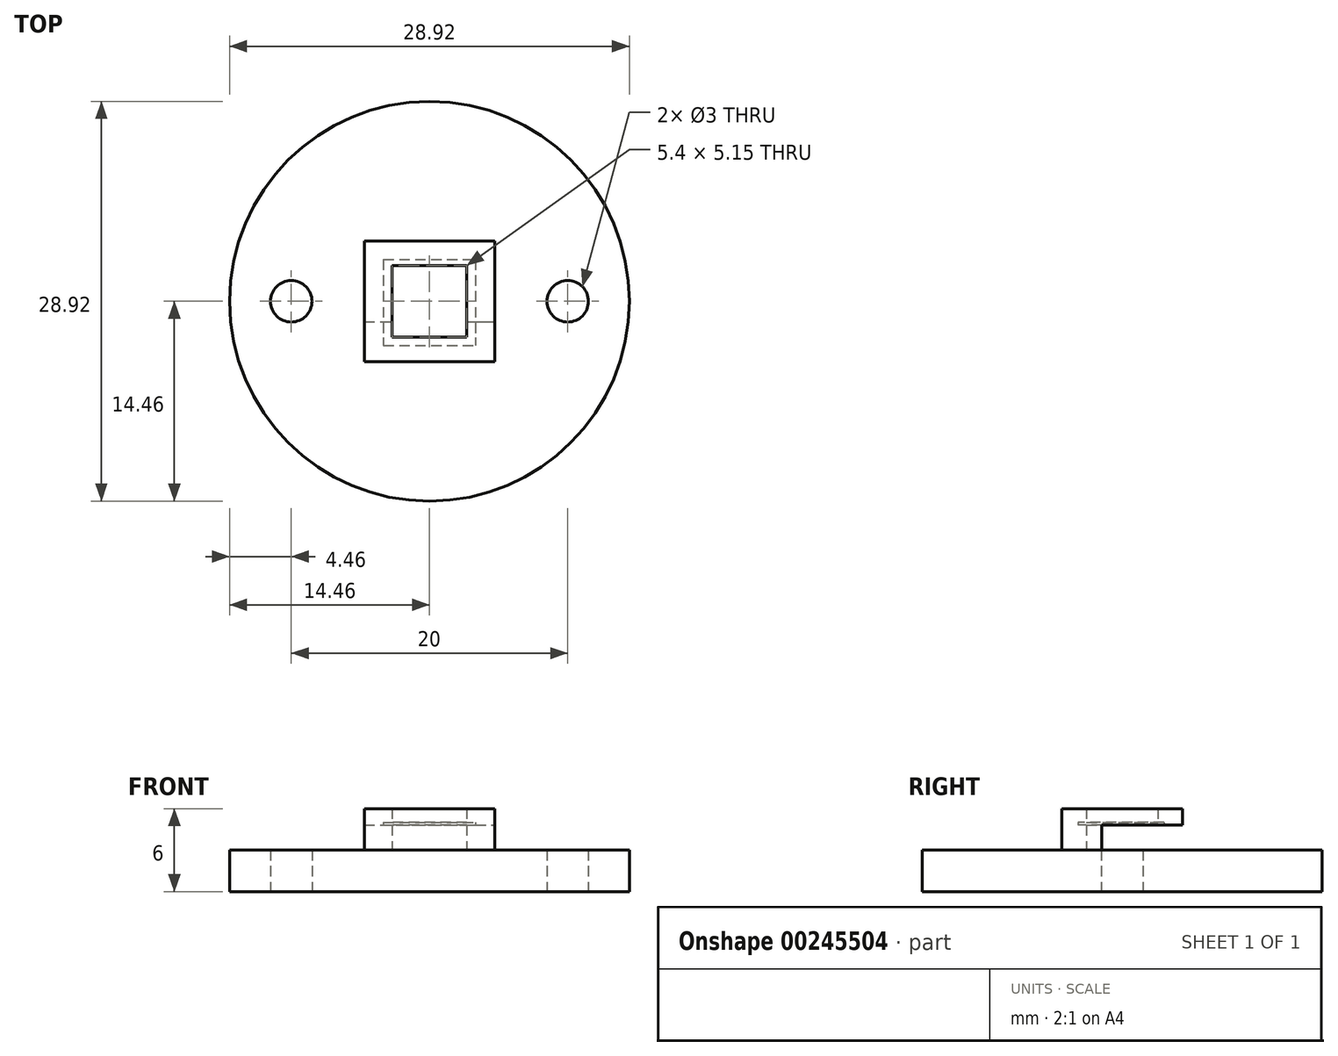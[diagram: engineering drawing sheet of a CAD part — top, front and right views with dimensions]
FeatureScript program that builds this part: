
annotation { "Feature Type Name" : "Feature", "Feature Type Description" : "" }
export const myFeature = defineFeature(function(context is Context, id is Id, definition is map)
    precondition{}
    {
        {
            var Q0;
            Q0=qCreatedBy(makeId("Top.planeOp"),FACE);
            var sketch = newSketch(context, id + "F0", { "sketchPlane" : qUnion([Q0])});
            skPoint(sketch, "E0", {"position": v(10, 0) * mm});
            skPoint(sketch, "E1", {"position": v(-10, 0) * mm});
            skCircle(sketch, "E2", {"center": v(0, 0) * mm, "radius": 14.46 * mm});
            skCircle(sketch, "E3", {"center": v(-10, 0) * mm, "radius": 1.5 * mm});
            skCircle(sketch, "E4", {"center": v(10, 0) * mm, "radius": 1.5 * mm});
            skSolve(sketch);
        }
        {
            var Q0;
            Q0 = qSketchRegion(id + "F0", true);
            extrude(context, id + "F1", {"entities" : qUnion([Q0]), "depth" : 3 * mm});
        }
        {
            var Q0;
            Q0=makeQuery(id+"F1.opExtrude","CAP_FACE",FACE,{"disambiguationData":[OSD([sQuery(id+"F0.wireOp",EDGE,"E2"),sQuery(id+"F0.wireOp",EDGE,"E3"),sQuery(id+"F0.wireOp",EDGE,"E4")])],"isStart":false});
            var sketch = newSketch(context, id + "F2", { "sketchPlane" : qUnion([Q0])});
            skLineSegment(sketch, "E5.bottom", {"start": v(-4.71, 4.36) * mm, "end": v(4.71, 4.36) * mm});
            skLineSegment(sketch, "E5.top", {"start": v(-4.71, -4.36) * mm, "end": v(4.71, -4.36) * mm});
            skLineSegment(sketch, "E5.left", {"start": v(-4.71, 4.36) * mm, "end": v(-4.71, -4.36) * mm});
            skLineSegment(sketch, "E5.right", {"start": v(4.71, 4.36) * mm, "end": v(4.71, -4.36) * mm});
            skLineSegment(sketch, "E6.bottom", {"start": v(-2.7, 2.58) * mm, "end": v(2.7, 2.58) * mm});
            skLineSegment(sketch, "E6.top", {"start": v(-2.7, -2.58) * mm, "end": v(2.7, -2.58) * mm});
            skLineSegment(sketch, "E6.left", {"start": v(-2.7, 2.58) * mm, "end": v(-2.7, -2.58) * mm});
            skLineSegment(sketch, "E6.right", {"start": v(2.7, 2.58) * mm, "end": v(2.7, -2.58) * mm});
            skSolve(sketch);
        }
        {
            var Q0;
            Q0 = qSketchRegion(id + "F2", true);
            extrude(context, id + "F3", {"entities" : qUnion([Q0]), "operationType" : NewBodyOperationType.ADD, "depth" : 3 * mm});
        }
        {
            var Q0;
            {var subQ0=sQuery(id+"F0.wireOp",EDGE,"E4");var subQ1=sQuery(id+"F0.wireOp",EDGE,"E3");var subQ2=sQuery(id+"F0.wireOp",EDGE,"E2");Q0=makeQuery(id+"F3.boolean.opBoolean","SPLIT",FACE,{"disambiguationData":[TD([makeQuery(id+"F1.opExtrude","SWEPT_FACE",FACE,{"disambiguationData":[OSD([subQ2])]})])],"derivedFrom":makeQuery(id+"F1.opExtrude","CAP_FACE",FACE,{"disambiguationData":[OSD([subQ2,subQ1,subQ0])],"isStart":false})});}
            var sketch = newSketch(context, id + "F4", { "sketchPlane" : qUnion([Q0])});
            skLineSegment(sketch, "E7.bottom", {"start": v(-8.33, 6.23) * mm, "end": v(7.6, 6.23) * mm});
            skLineSegment(sketch, "E7.top", {"start": v(-8.33, -1.47) * mm, "end": v(7.6, -1.47) * mm});
            skLineSegment(sketch, "E7.left", {"start": v(-8.33, 6.23) * mm, "end": v(-8.33, -1.47) * mm});
            skLineSegment(sketch, "E7.right", {"start": v(7.6, 6.23) * mm, "end": v(7.6, -1.47) * mm});
            skSolve(sketch);
        }
        {
            var Q0;
            Q0 = qSketchRegion(id + "F4", true);
            extrude(context, id + "F5", {"entities" : qUnion([Q0]), "operationType" : NewBodyOperationType.REMOVE, "depth" : 1.8 * mm});
        }
        {
            var Q0;
            Q0=makeQuery(id+"F5.boolean.opBoolean","COPY",FACE,{"derivedFrom":makeQuery(id+"F5.opExtrude","CAP_FACE",FACE,{"disambiguationData":[OSD([sQuery(id+"F4.wireOp",EDGE,"E7.bottom"),sQuery(id+"F4.wireOp",EDGE,"E7.top"),sQuery(id+"F4.wireOp",EDGE,"E7.left"),sQuery(id+"F4.wireOp",EDGE,"E7.right")])],"isStart":false})});
            var sketch = newSketch(context, id + "F6", { "sketchPlane" : qUnion([Q0])});
            skLineSegment(sketch, "E8.bottom", {"start": v(-3.33, -3.03) * mm, "end": v(3.31, -3.03) * mm});
            skLineSegment(sketch, "E8.top", {"start": v(-3.33, 3.2) * mm, "end": v(3.31, 3.2) * mm});
            skLineSegment(sketch, "E8.left", {"start": v(-3.33, -3.03) * mm, "end": v(-3.33, 3.2) * mm});
            skLineSegment(sketch, "E8.right", {"start": v(3.31, -3.03) * mm, "end": v(3.31, 3.2) * mm});
            skSolve(sketch);
        }
        {
            var Q0;
            Q0 = qSketchRegion(id + "F6", true);
            extrude(context, id + "F7", {"entities" : qUnion([Q0]), "operationType" : NewBodyOperationType.REMOVE, "oppositeDirection" : true, "depth" : 0.2 * mm});
        }
    });
